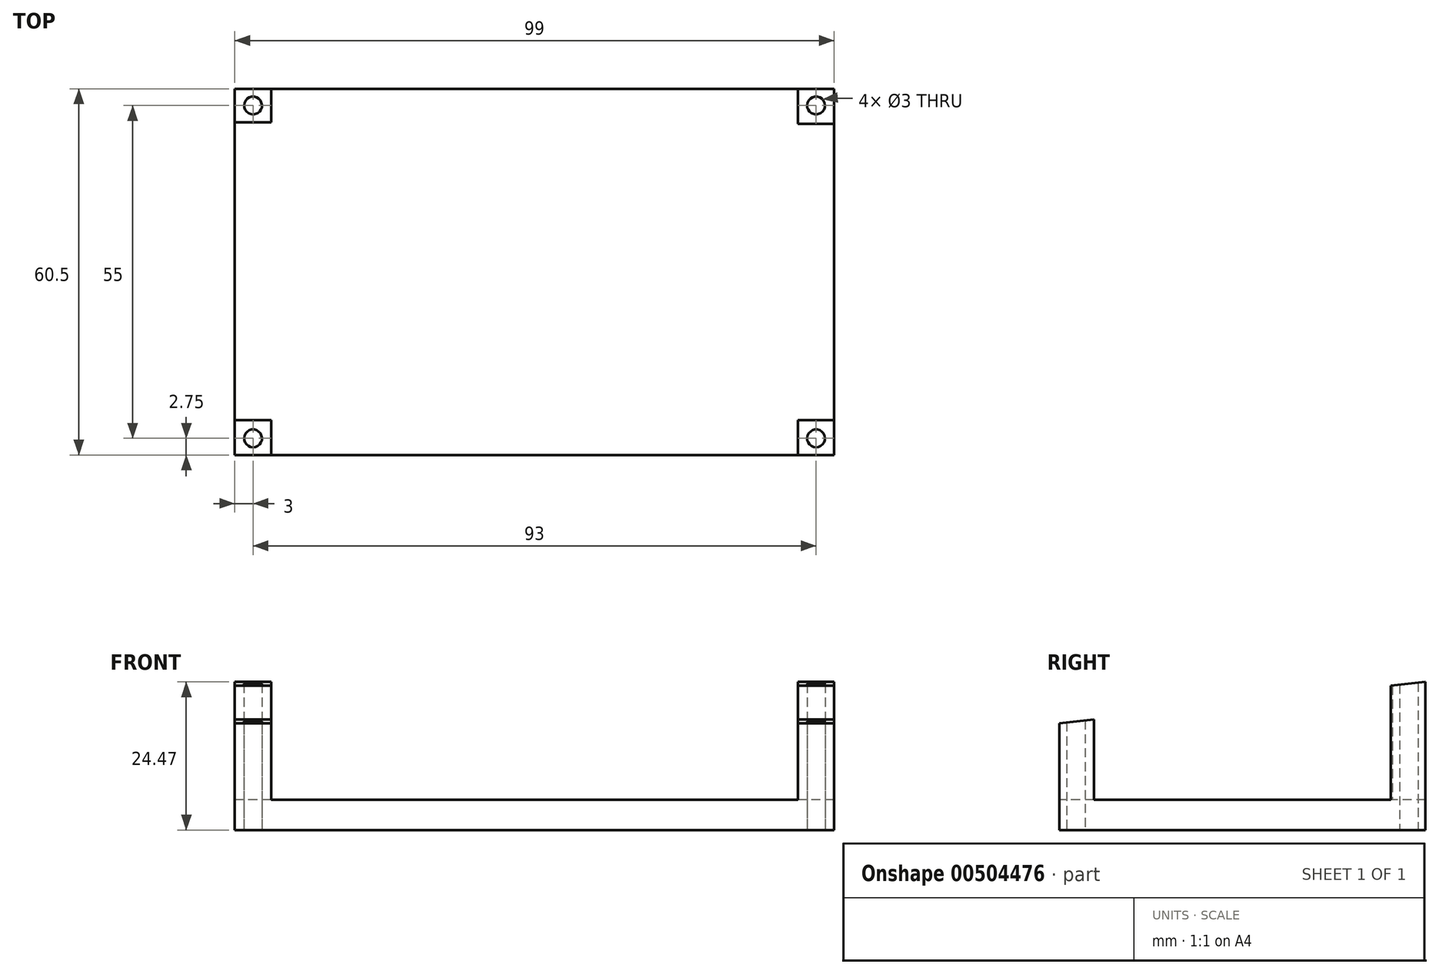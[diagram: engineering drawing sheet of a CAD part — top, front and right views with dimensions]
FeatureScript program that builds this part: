
annotation { "Feature Type Name" : "Feature", "Feature Type Description" : "" }
export const myFeature = defineFeature(function(context is Context, id is Id, definition is map)
    precondition{}
    {
        {
            var Q0;
            Q0=qCreatedBy(makeId("Top.planeOp"),FACE);
            var sketch = newSketch(context, id + "F0", { "sketchPlane" : qUnion([Q0])});
            skLineSegment(sketch, "E0.bottom", {"start": v(-49.5, 30.25) * mm, "end": v(49.5, 30.25) * mm});
            skLineSegment(sketch, "E0.top", {"start": v(-49.5, -30.25) * mm, "end": v(49.5, -30.25) * mm});
            skLineSegment(sketch, "E0.left", {"start": v(-49.5, 30.25) * mm, "end": v(-49.5, -30.25) * mm});
            skLineSegment(sketch, "E0.right", {"start": v(49.5, 30.25) * mm, "end": v(49.5, -30.25) * mm});
            skPoint(sketch, "E0.middle", {"position": v(0, 0) * mm});
            skLineSegment(sketch, "E1.bottom", {"start": v(48.75, -20.99) * mm, "end": v(-48.75, -20.99) * mm, "construction": true});
            skLineSegment(sketch, "E1.top", {"start": v(48.75, 19.01) * mm, "end": v(-48.75, 19.01) * mm, "construction": true});
            skLineSegment(sketch, "E1.left", {"start": v(48.75, -20.99) * mm, "end": v(48.75, 19.01) * mm, "construction": true});
            skLineSegment(sketch, "E1.right", {"start": v(-48.75, -20.99) * mm, "end": v(-48.75, 19.01) * mm, "construction": true});
            skPoint(sketch, "E1.middle", {"position": v(0, -0.99) * mm});
            skLineSegment(sketch, "E2.bottom", {"start": v(46.5, -27.5) * mm, "end": v(-46.5, -27.5) * mm, "construction": true});
            skLineSegment(sketch, "E2.top", {"start": v(46.5, 27.5) * mm, "end": v(-46.5, 27.5) * mm, "construction": true});
            skLineSegment(sketch, "E2.left", {"start": v(46.5, -27.5) * mm, "end": v(46.5, 27.5) * mm, "construction": true});
            skLineSegment(sketch, "E2.right", {"start": v(-46.5, -27.5) * mm, "end": v(-46.5, 27.5) * mm, "construction": true});
            skCircle(sketch, "E3", {"center": v(-46.5, 27.5) * mm, "radius": 1.5 * mm});
            skCircle(sketch, "E4", {"center": v(46.5, 27.5) * mm, "radius": 1.5 * mm});
            skCircle(sketch, "E5", {"center": v(-46.5, -27.5) * mm, "radius": 1.5 * mm});
            skCircle(sketch, "E6", {"center": v(46.5, -27.5) * mm, "radius": 1.5 * mm});
            skLineSegment(sketch, "E7", {"start": v(-43.5, 30.25) * mm, "end": v(-43.5, 24.75) * mm});
            skLineSegment(sketch, "E8", {"start": v(-43.5, 24.75) * mm, "end": v(-49.5, 24.75) * mm});
            skLineSegment(sketch, "E9", {"start": v(-49.5, -24.5) * mm, "end": v(-43.5, -24.5) * mm});
            skLineSegment(sketch, "E10", {"start": v(-43.5, -24.5) * mm, "end": v(-43.5, -30.25) * mm});
            skLineSegment(sketch, "E11", {"start": v(49.5, -24.5) * mm, "end": v(43.5, -24.5) * mm});
            skLineSegment(sketch, "E12", {"start": v(43.5, -24.5) * mm, "end": v(43.5, -30.25) * mm});
            skLineSegment(sketch, "E13", {"start": v(43.5, 30.25) * mm, "end": v(43.5, 24.5) * mm});
            skLineSegment(sketch, "E14", {"start": v(43.5, 24.5) * mm, "end": v(49.5, 24.5) * mm});
            skSolve(sketch);
        }
        {
            var Q0;
            {var subQ3=sQuery(id+"F0.wireOp",EDGE,"E7");Q0=makeQuery(id+"F0.imprint","IMPRINT",FACE,{"disambiguationData":[TD([[makeQuery(id+"F0.imprint","IMPRINT",EDGE,{"derivedFrom":subQ3}),1.0]])]});}
            extrude(context, id + "F1", {"entities" : qUnion([Q0]), "depth" : 5 * mm});
        }
        {
            var Q0;
            Q0=makeQuery(id+"F0.imprint","IMPRINT",FACE,{"disambiguationData":[TD([[makeQuery(id+"F0.imprint","IMPRINT",EDGE,{"derivedFrom":sQuery(id+"F0.wireOp",EDGE,"E3")}),-1.0]])]});
            var Q1;
            Q1=makeQuery(id+"F0.imprint","IMPRINT",FACE,{"disambiguationData":[TD([[makeQuery(id+"F0.imprint","IMPRINT",EDGE,{"derivedFrom":sQuery(id+"F0.wireOp",EDGE,"E5")}),-1.0]])]});
            var Q2;
            Q2=makeQuery(id+"F0.imprint","IMPRINT",FACE,{"disambiguationData":[TD([[makeQuery(id+"F0.imprint","IMPRINT",EDGE,{"derivedFrom":sQuery(id+"F0.wireOp",EDGE,"E6")}),-1.0]])]});
            var Q3;
            Q3=makeQuery(id+"F0.imprint","IMPRINT",FACE,{"disambiguationData":[TD([[makeQuery(id+"F0.imprint","IMPRINT",EDGE,{"derivedFrom":sQuery(id+"F0.wireOp",EDGE,"E4")}),-1.0]])]});
            extrude(context, id + "F2", {"entities" : qUnion([Q0, Q1, Q2, Q3]), "operationType" : NewBodyOperationType.ADD, "depth" : 25 * mm});
        }
        {
            var Q0;
            {var subQ0=sQuery(id+"F0.wireOp",EDGE,"E0.right");Q0=makeQuery(id+"F2.boolean.opBoolean","MERGE",FACE,{"derivedFrom":[makeQuery(id+"F1.opExtrude","SWEPT_FACE",FACE,{"disambiguationData":[OSD([subQ0])]}),makeQuery(id+"F2.opExtrude","SWEPT_FACE",FACE,{"disambiguationData":[OSD([subQ0]),TDD([makeQuery(id+"F0.imprint","IMPRINT",EDGE,{"disambiguationData":[TD([[makeQuery(id+"F0.imprint","INTERSECT",VERTEX,{"derivedFrom":[sQuery(id+"F0.wireOp",EDGE,"E0.bottom"),subQ0]}),-1.0]])],"derivedFrom":subQ0})])]}),makeQuery(id+"F2.opExtrude","SWEPT_FACE",FACE,{"disambiguationData":[OSD([subQ0]),TDD([makeQuery(id+"F0.imprint","IMPRINT",EDGE,{"disambiguationData":[TD([[makeQuery(id+"F0.imprint","INTERSECT",VERTEX,{"derivedFrom":[sQuery(id+"F0.wireOp",EDGE,"E0.top"),subQ0]}),1.0]])],"derivedFrom":subQ0})])]})]});}
            var sketch = newSketch(context, id + "F3", { "sketchPlane" : qUnion([Q0])});
            skLineSegment(sketch, "E15", {"start": v(34.54, 31.62) * mm, "end": v(-33.88, 31.62) * mm});
            skLineSegment(sketch, "E16", {"start": v(-33.88, 31.62) * mm, "end": v(-33.88, 17.22) * mm});
            skLineSegment(sketch, "E17", {"start": v(-33.88, 17.22) * mm, "end": v(34.92, 25) * mm});
            skLineSegment(sketch, "E18", {"start": v(34.92, 25) * mm, "end": v(34.54, 31.62) * mm});
            skSolve(sketch);
        }
        {
            var Q0;
            Q0 = qSketchRegion(id + "F3", true);
            extrude(context, id + "F4", {"entities" : qUnion([Q0]), "operationType" : NewBodyOperationType.REMOVE, "oppositeDirection" : true, "depth" : 105 * mm});
        }
    });
